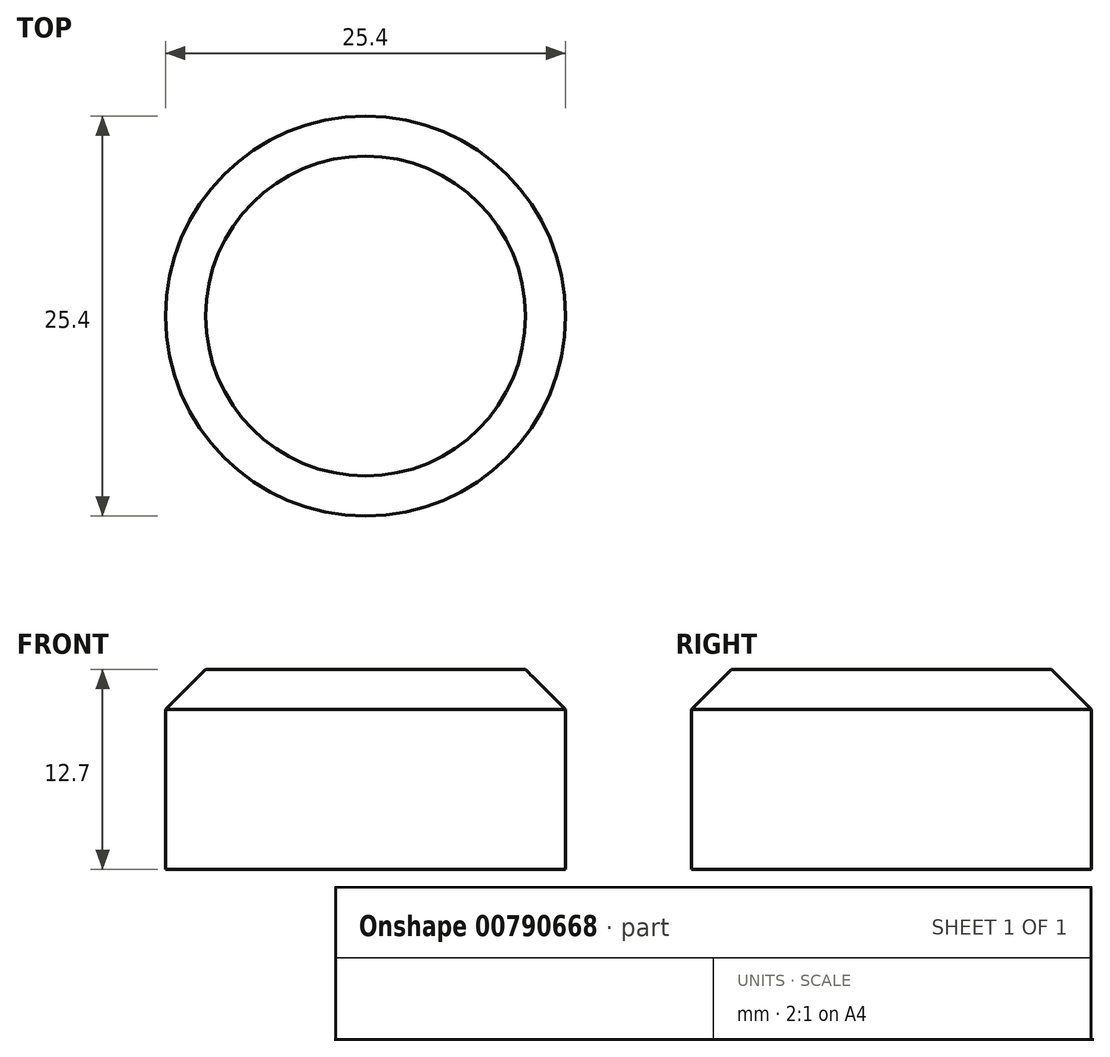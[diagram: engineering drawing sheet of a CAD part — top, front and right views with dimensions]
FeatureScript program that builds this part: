
annotation { "Feature Type Name" : "Feature", "Feature Type Description" : "" }
export const myFeature = defineFeature(function(context is Context, id is Id, definition is map)
    precondition{}
    {
        {
            var Q0;
            Q0=qCreatedBy(makeId("Top.planeOp"),FACE);
            var sketch = newSketch(context, id + "F0", { "sketchPlane" : qUnion([Q0])});
            skCircle(sketch, "E0", {"center": v(0, 0) * mm, "radius": 12.7 * mm});
            skSolve(sketch);
        }
        {
            var Q0;
            Q0 = qSketchRegion(id + "F0", true);
            extrude(context, id + "F1", {"entities" : qUnion([Q0]), "depth" : 12.7 * mm, "offsetDistance" : 25.4 * mm});
        }
        {
            var Q0;
            Q0=makeQuery(id+"F1.opExtrude","CAP_FACE",FACE,{"disambiguationData":[OSD([sQuery(id+"F0.wireOp",EDGE,"E0")])],"isStart":false});
            chamfer(context, id + "F2", {"entities" : qUnion([Q0]), "width" : 2.54 * mm, "tangentPropagation" : true});
        }
    });
